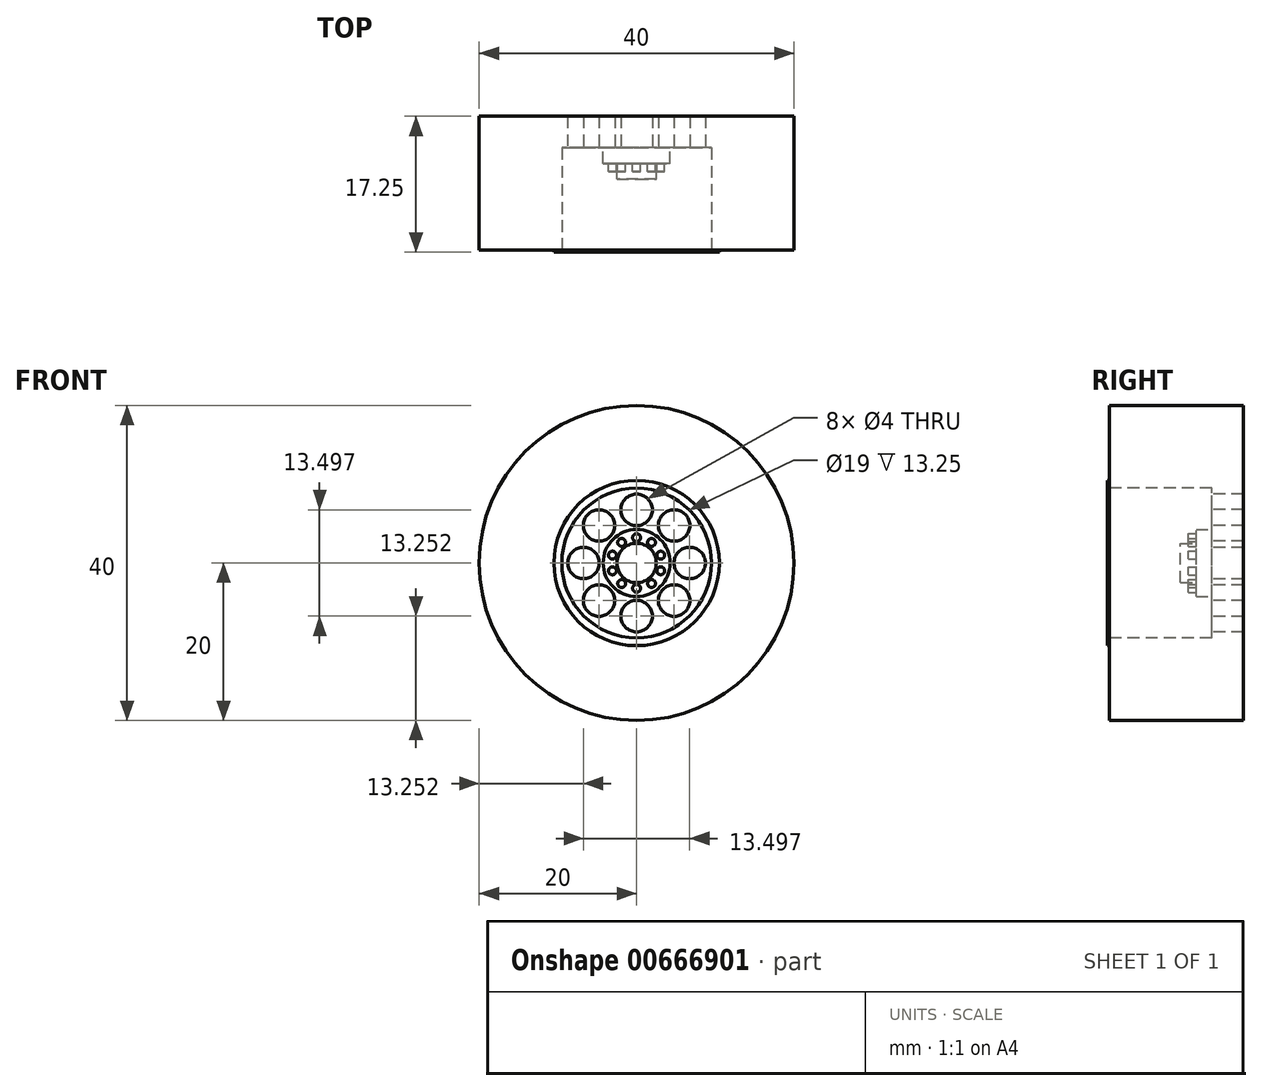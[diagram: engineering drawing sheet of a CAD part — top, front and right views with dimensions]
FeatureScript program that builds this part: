
annotation { "Feature Type Name" : "Feature", "Feature Type Description" : "" }
export const myFeature = defineFeature(function(context is Context, id is Id, definition is map)
    precondition{}
    {
        {
            var Q0;
            Q0=qCreatedBy(makeId("Front.planeOp"),FACE);
            var sketch = newSketch(context, id + "F0", { "sketchPlane" : qUnion([Q0])});
            skCircle(sketch, "E0", {"center": v(0, 0) * mm, "radius": 20 * mm});
            skSolve(sketch);
        }
        {
            var Q0;
            Q0=makeQuery(id+"F0.imprint","IMPRINT",FACE,{"disambiguationData":[TD([[makeQuery(id+"F0.imprint","IMPRINT",EDGE,{"derivedFrom":sQuery(id+"F0.wireOp",EDGE,"E0")}),1.0]])]});
            extrude(context, id + "F1", {"entities" : qUnion([Q0]), "depth" : 17 * mm, "offsetDistance" : 25 * mm});
        }
        {
            var Q0;
            Q0=makeQuery(id+"F1.opExtrude","CAP_FACE",FACE,{"disambiguationData":[OSD([sQuery(id+"F0.wireOp",EDGE,"E0")])],"isStart":false});
            var sketch = newSketch(context, id + "F2", { "sketchPlane" : qUnion([Q0])});
            skCircle(sketch, "E1", {"center": v(0, 0) * mm, "radius": 9.5 * mm});
            skCircle(sketch, "E2", {"center": v(0, 0) * mm, "radius": 10.5 * mm});
            skSolve(sketch);
        }
        {
            var Q0;
            Q0=makeQuery(id+"F2.imprint","IMPRINT",FACE,{"disambiguationData":[TD([[makeQuery(id+"F2.imprint","IMPRINT",EDGE,{"derivedFrom":sQuery(id+"F2.wireOp",EDGE,"E1")}),1.0]])]});
            extrude(context, id + "F3", {"entities" : qUnion([Q0]), "operationType" : NewBodyOperationType.REMOVE, "oppositeDirection" : true, "depth" : 13 * mm, "offsetDistance" : 25 * mm});
        }
        {
            var Q0;
            Q0 = qSketchRegion(id + "F2", true);
            extrude(context, id + "F4", {"entities" : qUnion([Q0]), "operationType" : NewBodyOperationType.ADD, "depth" : .25 * mm, "offsetDistance" : 25 * mm});
        }
        {
            var Q0;
            Q0=makeQuery(id+"F3.boolean.opBoolean","COPY",FACE,{"derivedFrom":makeQuery(id+"F3.opExtrude","CAP_FACE",FACE,{"disambiguationData":[OSD([sQuery(id+"F2.wireOp",EDGE,"E1")])],"isStart":false})});
            var sketch = newSketch(context, id + "F5", { "sketchPlane" : qUnion([Q0])});
            skCircle(sketch, "E3", {"center": v(0, 6.75) * mm, "radius": 2 * mm});
            skCircle(sketch, "E4.1.0", {"center": v(-4.77, 4.77) * mm, "radius": 2 * mm});
            skCircle(sketch, "E4.2.0", {"center": v(-6.75, 0) * mm, "radius": 2 * mm});
            skCircle(sketch, "E4.3.0", {"center": v(-4.77, -4.77) * mm, "radius": 2 * mm});
            skCircle(sketch, "E4.4.0", {"center": v(0, -6.75) * mm, "radius": 2 * mm});
            skCircle(sketch, "E4.5.0", {"center": v(4.77, -4.77) * mm, "radius": 2 * mm});
            skCircle(sketch, "E4.6.0", {"center": v(6.75, 0) * mm, "radius": 2 * mm});
            skCircle(sketch, "E4.7.0", {"center": v(4.77, 4.77) * mm, "radius": 2 * mm});
            skPoint(sketch, "E4.center", {"position": v(0, 0) * mm});
            skSolve(sketch);
        }
        {
            var Q0;
            Q0=makeQuery(id+"F5.imprint","IMPRINT",FACE,{"disambiguationData":[TD([[makeQuery(id+"F5.imprint","IMPRINT",EDGE,{"derivedFrom":sQuery(id+"F5.wireOp",EDGE,"E3")}),1.0]])]});
            var Q1;
            Q1=makeQuery(id+"F5.imprint","IMPRINT",FACE,{"disambiguationData":[TD([[makeQuery(id+"F5.imprint","IMPRINT",EDGE,{"derivedFrom":sQuery(id+"F5.wireOp",EDGE,"E4.7.0")}),1.0]])]});
            var Q2;
            Q2=makeQuery(id+"F5.imprint","IMPRINT",FACE,{"disambiguationData":[TD([[makeQuery(id+"F5.imprint","IMPRINT",EDGE,{"derivedFrom":sQuery(id+"F5.wireOp",EDGE,"E4.6.0")}),1.0]])]});
            var Q3;
            Q3=makeQuery(id+"F5.imprint","IMPRINT",FACE,{"disambiguationData":[TD([[makeQuery(id+"F5.imprint","IMPRINT",EDGE,{"derivedFrom":sQuery(id+"F5.wireOp",EDGE,"E4.5.0")}),1.0]])]});
            var Q4;
            Q4=makeQuery(id+"F5.imprint","IMPRINT",FACE,{"disambiguationData":[TD([[makeQuery(id+"F5.imprint","IMPRINT",EDGE,{"derivedFrom":sQuery(id+"F5.wireOp",EDGE,"E4.4.0")}),1.0]])]});
            var Q5;
            Q5=makeQuery(id+"F5.imprint","IMPRINT",FACE,{"disambiguationData":[TD([[makeQuery(id+"F5.imprint","IMPRINT",EDGE,{"derivedFrom":sQuery(id+"F5.wireOp",EDGE,"E4.3.0")}),1.0]])]});
            var Q6;
            Q6=makeQuery(id+"F5.imprint","IMPRINT",FACE,{"disambiguationData":[TD([[makeQuery(id+"F5.imprint","IMPRINT",EDGE,{"derivedFrom":sQuery(id+"F5.wireOp",EDGE,"E4.2.0")}),1.0]])]});
            var Q7;
            Q7=makeQuery(id+"F5.imprint","IMPRINT",FACE,{"disambiguationData":[TD([[makeQuery(id+"F5.imprint","IMPRINT",EDGE,{"derivedFrom":sQuery(id+"F5.wireOp",EDGE,"E4.1.0")}),1.0]])]});
            extrude(context, id + "F6", {"entities" : qUnion([Q0, Q1, Q2, Q3, Q4, Q5, Q6, Q7]), "operationType" : NewBodyOperationType.REMOVE, "oppositeDirection" : true, "depth" : 25 * mm, "offsetDistance" : 25 * mm});
        }
        {
            var Q0;
            Q0=makeQuery(id+"F3.boolean.opBoolean","COPY",FACE,{"derivedFrom":makeQuery(id+"F3.opExtrude","CAP_FACE",FACE,{"disambiguationData":[OSD([sQuery(id+"F2.wireOp",EDGE,"E1")])],"isStart":false})});
            var sketch = newSketch(context, id + "F7", { "sketchPlane" : qUnion([Q0])});
            skCircle(sketch, "E5", {"center": v(0, 0) * mm, "radius": 4.25 * mm});
            skSolve(sketch);
        }
        {
            var Q0;
            Q0=makeQuery(id+"F7.imprint","IMPRINT",FACE,{"disambiguationData":[TD([[makeQuery(id+"F7.imprint","IMPRINT",EDGE,{"derivedFrom":sQuery(id+"F7.wireOp",EDGE,"E5")}),1.0]])]});
            extrude(context, id + "F8", {"entities" : qUnion([Q0]), "operationType" : NewBodyOperationType.ADD, "depth" : 2 * mm, "offsetDistance" : 25 * mm});
        }
        {
            var Q0;
            Q0=makeQuery(id+"F8.opExtrude","CAP_FACE",FACE,{"disambiguationData":[OSD([sQuery(id+"F7.wireOp",EDGE,"E5")])],"isStart":false});
            var sketch = newSketch(context, id + "F9", { "sketchPlane" : qUnion([Q0])});
            skCircle(sketch, "E6", {"center": v(0, 0) * mm, "radius": 2.5 * mm});
            skSolve(sketch);
        }
        {
            var Q0;
            Q0=makeQuery(id+"F9.imprint","IMPRINT",FACE,{"disambiguationData":[TD([[makeQuery(id+"F9.imprint","IMPRINT",EDGE,{"derivedFrom":sQuery(id+"F9.wireOp",EDGE,"E6")}),1.0]])]});
            var Q1;
            Q1 = qSketchRegion(id + "F11", true);
            extrude(context, id + "F10", {"entities" : qUnion([Q0, Q1]), "operationType" : NewBodyOperationType.ADD, "depth" : 2 * mm, "offsetDistance" : 25 * mm});
        }
        {
            var Q0;
            Q0=makeQuery(id+"F8.opExtrude","CAP_FACE",FACE,{"disambiguationData":[OSD([sQuery(id+"F7.wireOp",EDGE,"E5")])],"isStart":false});
            var sketch = newSketch(context, id + "F11", { "sketchPlane" : qUnion([Q0])});
            skCircle(sketch, "E7", {"center": v(0, 3.23) * mm, "radius": 0.5 * mm});
            skCircle(sketch, "E8.1.0", {"center": v(-1.9, 2.61) * mm, "radius": 0.5 * mm});
            skCircle(sketch, "E8.2.0", {"center": v(-3.07, 1) * mm, "radius": 0.5 * mm});
            skCircle(sketch, "E8.3.0", {"center": v(-3.07, -1) * mm, "radius": 0.5 * mm});
            skCircle(sketch, "E8.4.0", {"center": v(-1.9, -2.61) * mm, "radius": 0.5 * mm});
            skCircle(sketch, "E8.5.0", {"center": v(0, -3.23) * mm, "radius": 0.5 * mm});
            skCircle(sketch, "E8.6.0", {"center": v(1.9, -2.61) * mm, "radius": 0.5 * mm});
            skCircle(sketch, "E8.7.0", {"center": v(3.07, -1) * mm, "radius": 0.5 * mm});
            skCircle(sketch, "E8.8.0", {"center": v(3.07, 1) * mm, "radius": 0.5 * mm});
            skCircle(sketch, "E8.9.0", {"center": v(1.9, 2.61) * mm, "radius": 0.5 * mm});
            skPoint(sketch, "E8.center", {"position": v(0, 0) * mm});
            skSolve(sketch);
        }
        {
            var Q0;
            Q0=makeQuery(id+"F11.imprint","IMPRINT",FACE,{"disambiguationData":[TD([[makeQuery(id+"F11.imprint","IMPRINT",EDGE,{"derivedFrom":sQuery(id+"F11.wireOp",EDGE,"E7")}),1.0]])]});
            var Q1;
            Q1=makeQuery(id+"F11.imprint","IMPRINT",FACE,{"disambiguationData":[TD([[makeQuery(id+"F11.imprint","IMPRINT",EDGE,{"derivedFrom":sQuery(id+"F11.wireOp",EDGE,"E8.9.0")}),1.0]])]});
            var Q2;
            Q2=makeQuery(id+"F11.imprint","IMPRINT",FACE,{"disambiguationData":[TD([[makeQuery(id+"F11.imprint","IMPRINT",EDGE,{"derivedFrom":sQuery(id+"F11.wireOp",EDGE,"E8.7.0")}),1.0]])]});
            var Q3;
            Q3=makeQuery(id+"F11.imprint","IMPRINT",FACE,{"disambiguationData":[TD([[makeQuery(id+"F11.imprint","IMPRINT",EDGE,{"derivedFrom":sQuery(id+"F11.wireOp",EDGE,"E8.8.0")}),1.0]])]});
            var Q4;
            Q4=makeQuery(id+"F11.imprint","IMPRINT",FACE,{"disambiguationData":[TD([[makeQuery(id+"F11.imprint","IMPRINT",EDGE,{"derivedFrom":sQuery(id+"F11.wireOp",EDGE,"E8.6.0")}),1.0]])]});
            var Q5;
            Q5=makeQuery(id+"F11.imprint","IMPRINT",FACE,{"disambiguationData":[TD([[makeQuery(id+"F11.imprint","IMPRINT",EDGE,{"derivedFrom":sQuery(id+"F11.wireOp",EDGE,"E8.5.0")}),1.0]])]});
            var Q6;
            Q6=makeQuery(id+"F11.imprint","IMPRINT",FACE,{"disambiguationData":[TD([[makeQuery(id+"F11.imprint","IMPRINT",EDGE,{"derivedFrom":sQuery(id+"F11.wireOp",EDGE,"E8.4.0")}),1.0]])]});
            var Q7;
            Q7=makeQuery(id+"F11.imprint","IMPRINT",FACE,{"disambiguationData":[TD([[makeQuery(id+"F11.imprint","IMPRINT",EDGE,{"derivedFrom":sQuery(id+"F11.wireOp",EDGE,"E8.3.0")}),1.0]])]});
            var Q8;
            Q8=makeQuery(id+"F11.imprint","IMPRINT",FACE,{"disambiguationData":[TD([[makeQuery(id+"F11.imprint","IMPRINT",EDGE,{"derivedFrom":sQuery(id+"F11.wireOp",EDGE,"E8.2.0")}),1.0]])]});
            var Q9;
            Q9=makeQuery(id+"F11.imprint","IMPRINT",FACE,{"disambiguationData":[TD([[makeQuery(id+"F11.imprint","IMPRINT",EDGE,{"derivedFrom":sQuery(id+"F11.wireOp",EDGE,"E8.1.0")}),1.0]])]});
            extrude(context, id + "F12", {"entities" : qUnion([Q0, Q1, Q2, Q3, Q4, Q5, Q6, Q7, Q8, Q9]), "operationType" : NewBodyOperationType.ADD, "depth" : 1 * mm, "offsetDistance" : 25 * mm});
        }
    });
